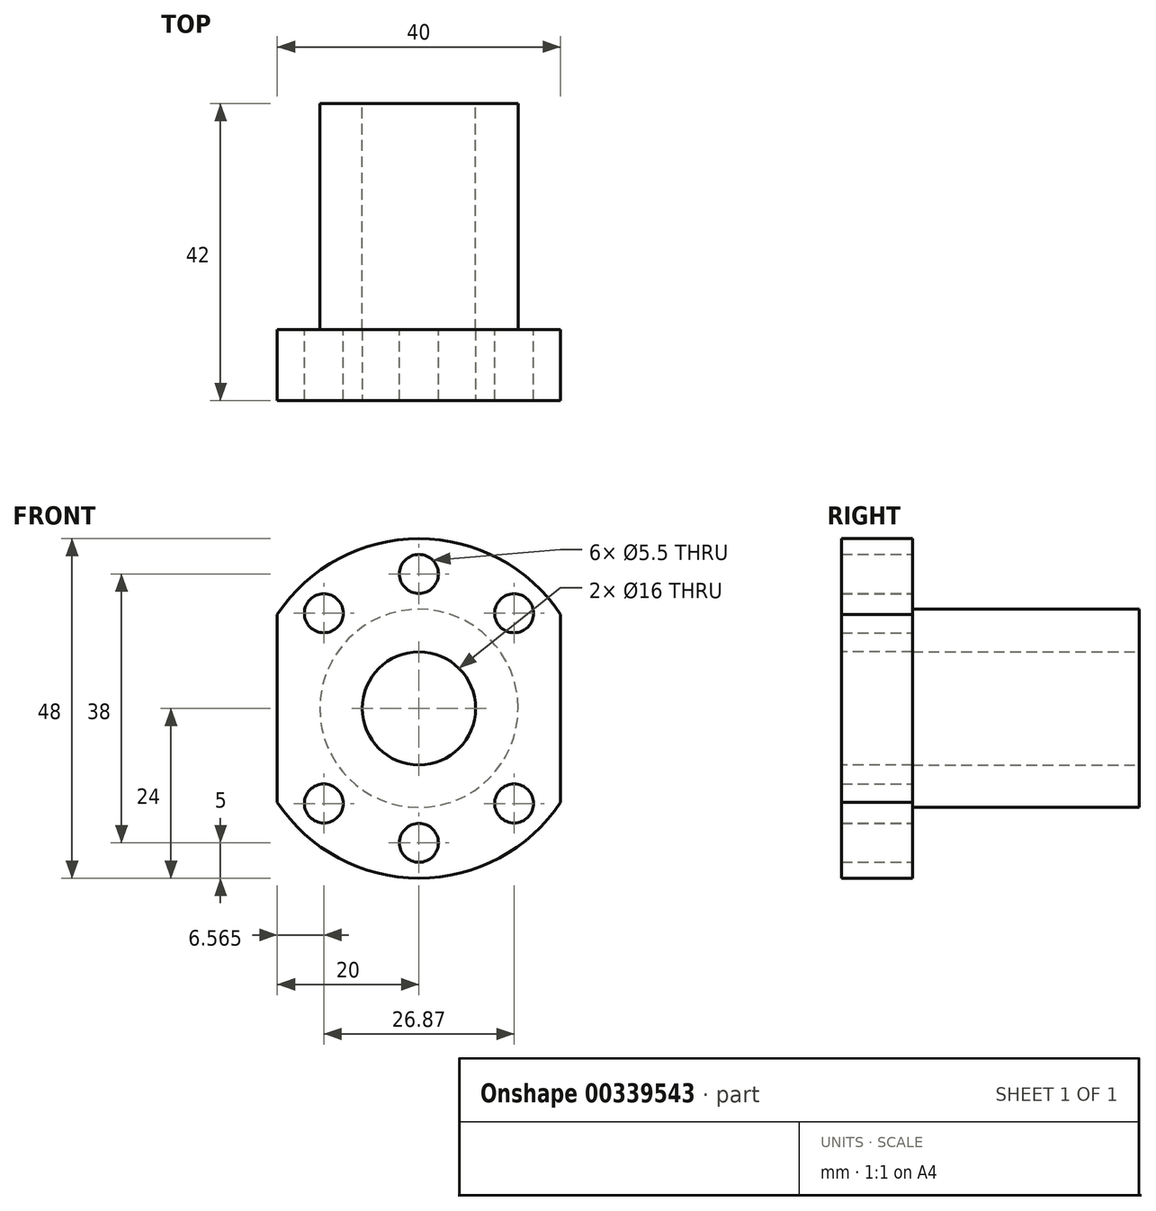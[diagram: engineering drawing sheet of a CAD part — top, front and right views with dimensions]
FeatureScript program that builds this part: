
annotation { "Feature Type Name" : "Feature", "Feature Type Description" : "" }
export const myFeature = defineFeature(function(context is Context, id is Id, definition is map)
    precondition{}
    {
        {
            var Q0;
            Q0=qCreatedBy(makeId("Front.planeOp"),FACE);
            var sketch = newSketch(context, id + "F0", { "sketchPlane" : qUnion([Q0])});
            skCircle(sketch, "E0", {"center": v(0, 0) * mm, "radius": 24 * mm});
            skCircle(sketch, "E1", {"center": v(0, 0) * mm, "radius": 14 * mm});
            skCircle(sketch, "E2", {"center": v(0, 0) * mm, "radius": 19 * mm});
            skCircle(sketch, "E3", {"center": v(-13.44, -13.44) * mm, "radius": 2.75 * mm});
            skCircle(sketch, "E4", {"center": v(0, -19) * mm, "radius": 2.75 * mm});
            skCircle(sketch, "E5", {"center": v(13.44, -13.44) * mm, "radius": 2.75 * mm});
            skCircle(sketch, "E6", {"center": v(0, 19) * mm, "radius": 2.75 * mm});
            skCircle(sketch, "E7", {"center": v(13.44, 13.44) * mm, "radius": 2.75 * mm});
            skLineSegment(sketch, "E8", {"start": v(0, 0) * mm, "end": v(0, 41.32) * mm, "construction": true});
            skLineSegment(sketch, "E9", {"start": v(0, 0) * mm, "end": v(0, -33.57) * mm, "construction": true});
            skLineSegment(sketch, "E10", {"start": v(0, 0) * mm, "end": v(-30.93, 30.93) * mm, "construction": true});
            skLineSegment(sketch, "E11", {"start": v(0, 0) * mm, "end": v(32.64, 32.64) * mm, "construction": true});
            skLineSegment(sketch, "E12", {"start": v(0, 0) * mm, "end": v(25.5, -25.5) * mm, "construction": true});
            skLineSegment(sketch, "E13", {"start": v(0, 0) * mm, "end": v(-26.87, -26.87) * mm, "construction": true});
            skLineSegment(sketch, "E14", {"start": v(0, 0) * mm, "end": v(0, -36.14) * mm, "construction": true});
            skCircle(sketch, "E15", {"center": v(-13.44, 13.44) * mm, "radius": 2.75 * mm});
            skLineSegment(sketch, "E16", {"start": v(20, 24.12) * mm, "end": v(20, -36.73) * mm});
            skLineSegment(sketch, "E17", {"start": v(-20, 20.56) * mm, "end": v(-20, -24.54) * mm});
            skSolve(sketch);
        }
        {
            var Q0;
            Q0=makeQuery(id+"F0.imprint","IMPRINT",FACE,{"disambiguationData":[TD([[makeQuery(id+"F0.imprint","IMPRINT",EDGE,{"derivedFrom":sQuery(id+"F0.wireOp",EDGE,"E1")}),1.0]])]});
            extrude(context, id + "F1", {"entities" : qUnion([Q0]), "oppositeDirection" : true, "depth" : 32 * mm});
        }
        {
            var Q0;
            Q0=makeQuery(id+"F0.imprint","IMPRINT",FACE,{"disambiguationData":[TD([[makeQuery(id+"F0.imprint","IMPRINT",EDGE,{"derivedFrom":sQuery(id+"F0.wireOp",EDGE,"E1")}),-1.0]])]});
            var Q1;
            {var subQ15=sQuery(id+"F0.wireOp",EDGE,"E0");var subQ24=sQuery(id+"F0.wireOp",EDGE,"E17");var subQ25=makeQuery(id+"F0.imprint","INTERSECT",VERTEX,{"disambiguationData":[OD(0.0)],"derivedFrom":[subQ15,subQ24]});Q1=makeQuery(id+"F0.imprint","IMPRINT",FACE,{"disambiguationData":[TD([[makeQuery(id+"F0.imprint","IMPRINT",EDGE,{"disambiguationData":[TD([[subQ25,1.0]])],"derivedFrom":subQ15}),1.0]])]});}
            var Q2;
            Q2=makeQuery(id+"F0.imprint","IMPRINT",FACE,{"disambiguationData":[TD([[makeQuery(id+"F0.imprint","IMPRINT",EDGE,{"derivedFrom":sQuery(id+"F0.wireOp",EDGE,"E1")}),1.0]])]});
            extrude(context, id + "F2", {"entities" : qUnion([Q0, Q1, Q2]), "depth" : 10 * mm});
        }
        {
            var Q0;
            Q0=sQuery(id+"F0.wireOp",VERTEX,"E13.start");
            var Q1;
            Q1=makeQuery(id+"F2.opExtrude","SWEPT_BODY",BODY,{"disambiguationData":[OSD([sQuery(id+"F0.wireOp",EDGE,"E0"),sQuery(id+"F0.wireOp",EDGE,"3Le320Qn-VjBY-srY0-ctTD-8nz4ECePLA43"),sQuery(id+"F0.wireOp",EDGE,"E3"),sQuery(id+"F0.wireOp",EDGE,"E4"),sQuery(id+"F0.wireOp",EDGE,"E5"),sQuery(id+"F0.wireOp",EDGE,"XYZcO0kG-A9sl-lWYi-Q1Rq-1tMAOFA1mSpu"),sQuery(id+"F0.wireOp",EDGE,"E6"),sQuery(id+"F0.wireOp",EDGE,"E7"),sQuery(id+"F0.wireOp",EDGE,"E15"),sQuery(id+"F0.wireOp",EDGE,"E16"),sQuery(id+"F0.wireOp",EDGE,"E17")])]});
            hole(context, id + "F3", {"style" : HoleStyle.SIMPLE, "endStyle" : HoleEndStyle.BLIND, "oppositeDirection" : true, "holeDiameter" : 16 * mm, "holeDepth" : 50 * mm, "isTappedThrough" : true, "tappedDepth" : 12 * mm, "tapClearance" : 3, "locations" : qUnion([Q0]), "scope" : qUnion([Q1])});
        }
        {
            var Q0;
            Q0=sQuery(id+"F0.wireOp",VERTEX,"E13.start");
            var Q1;
            Q1=makeQuery(id+"F1.opExtrude","SWEPT_BODY",BODY,{"disambiguationData":[OSD([sQuery(id+"F0.wireOp",EDGE,"E1")])]});
            hole(context, id + "F4", {"style" : HoleStyle.SIMPLE, "endStyle" : HoleEndStyle.BLIND, "holeDiameter" : 16 * mm, "holeDepth" : 50 * mm, "isTappedThrough" : true, "tappedDepth" : 12 * mm, "tapClearance" : 3, "locations" : qUnion([Q0]), "scope" : qUnion([Q1])});
        }
    });
